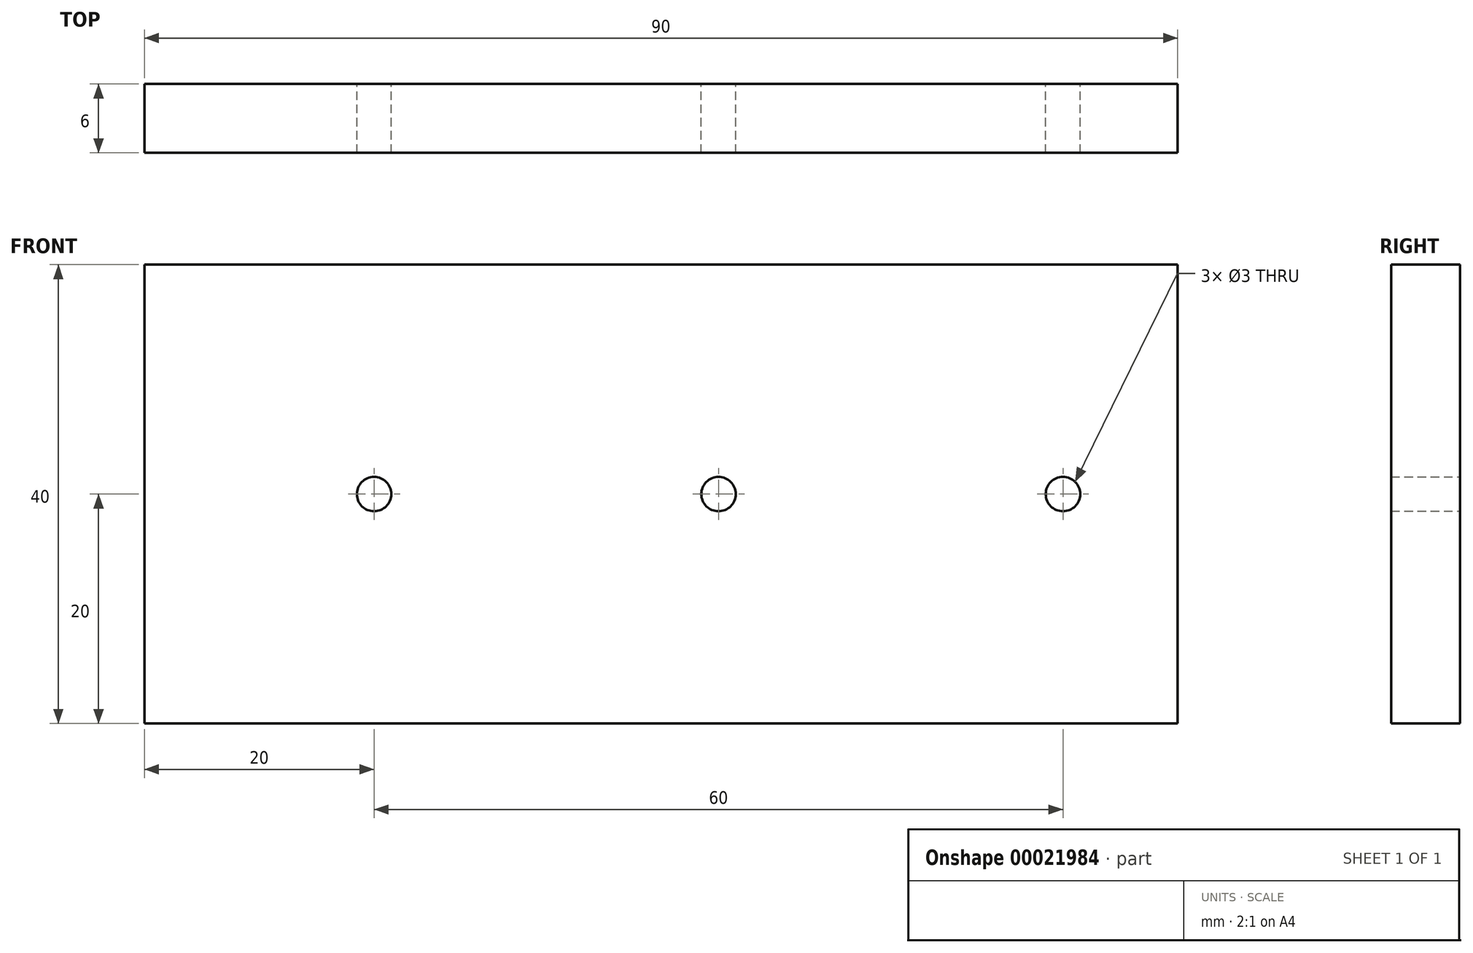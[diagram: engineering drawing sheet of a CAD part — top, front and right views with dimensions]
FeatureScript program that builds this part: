
annotation { "Feature Type Name" : "Feature", "Feature Type Description" : "" }
export const myFeature = defineFeature(function(context is Context, id is Id, definition is map)
    precondition{}
    {
        {
            var Q0;
            Q0=qCreatedBy(makeId("Front.planeOp"),FACE);
            var sketch = newSketch(context, id + "F0", { "sketchPlane" : qUnion([Q0])});
            skLineSegment(sketch, "E0.bottom", {"start": v(0, 0) * mm, "end": v(-90, 0) * mm});
            skLineSegment(sketch, "E0.top", {"start": v(0, 40) * mm, "end": v(-90, 40) * mm});
            skLineSegment(sketch, "E0.left", {"start": v(0, 0) * mm, "end": v(0, 40) * mm});
            skLineSegment(sketch, "E0.right", {"start": v(-90, 0) * mm, "end": v(-90, 40) * mm});
            skPoint(sketch, "E1", {"position": v(-90, 20) * mm});
            skPoint(sketch, "E2", {"position": v(-70, 20) * mm});
            skCircle(sketch, "E3", {"center": v(-70, 20) * mm, "radius": 1.5 * mm});
            skPoint(sketch, "E4", {"position": v(-40, 20) * mm});
            skCircle(sketch, "E5", {"center": v(-40, 20) * mm, "radius": 1.5 * mm});
            skCircle(sketch, "E6", {"center": v(-10, 20) * mm, "radius": 1.5 * mm});
            skPoint(sketch, "E7", {"position": v(0, 20) * mm});
            skSolve(sketch);
        }
        {
            var Q0;
            Q0 = qSketchRegion(id + "F0", true);
            extrude(context, id + "F1", {"entities" : qUnion([Q0]), "endBound" : BoundingType.SYMMETRIC, "depth" : 6 * mm});
        }
    });
